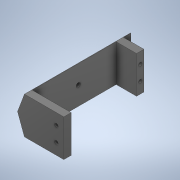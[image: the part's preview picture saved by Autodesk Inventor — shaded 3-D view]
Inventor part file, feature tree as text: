
AUTODESK INVENTOR PART (.ipt)
format: ipt  version: 2020 (Build 240168000, 168)  size: 239,616 bytes
history: native  units: in
note: dims shown in document units (in); Inventor stores cm internally (conversion verified against a paired STEP export)
features: sketch x9, extrude x7, projected_geometry x3, plane x1, loft x1
ambient origin geometry x8: Origin, YZ Plane, XZ Plane, XY Plane, X Axis, Y Axis, Z Axis, Center Point
bodies: Solid1 (feature_tree)
feature tree (21):
  sketch  "Sketch1"  dims[d1=1.1811in d2=3.3858in]
  plane  "Work Plane1"
  loft  "Loft1"
  extrude  "Extrusion1"  Depth=1.1811in
  extrude  "Extrusion2"  TaperAngle=0.0deg  [1 undecoded]
  extrude  "Extrusion3"  Depth=0.2362in
  extrude  "Extrusion4"  Depth=0.2362in
  extrude  "Extrusion5"  TaperAngle=0.0deg  [1 undecoded]
  extrude  "Extrusion6"  Depth=0.1378in
  extrude  "Extrusion7"  Depth=0.1378in
  sketch  "Sketch2"  dims[d3=1.1811in d5=0.5906in]
  sketch  "Sketch3"  dims[d6=0.5906in d7=0.0in d8=90.0deg]
  sketch  "Sketch4"  dims[d9=0.0in d10=90.0deg d11=0.2362in]
  sketch  "Sketch5"  dims[d12=0.2362in d13=0.2362in]
  projected_geometry  "Projected Loop1"
  sketch  "Sketch6"  dims[d14=0.65in d15=0.0in]
  projected_geometry  "Projected Loop2"
  sketch  "Sketch8"  dims[d16=1.7028in d17=0.1378in]
  sketch  "Sketch9"  dims[d18=0.0in d19=0.0in d20=0.1378in]
  sketch  "Sketch10"  dims[d21=0.1181in d22=0.0in d23=0.4724in d24=0.0in d25=0.1181in d26=0.1181in d27=0.2362in d28=0.2362in d29=0.1142in d30=0.1142in d31=0.2756in d32=0.0in d33=0.2362in d35=0.1181in d36=0.1181in d41=0.2756in d42=0.0in d43=0.1181in d44=0.2362in d45=0.2362in d46=0.1142in d47=0.1142in d48=0.1181in d49=0.1181in d50=0.0157in d51=0.5906in d52=0.0157in d53=0.2362in d54=0.1181in d55=0.0in d4=0.0197in]
  projected_geometry  "Projected Loop5"
note: 2 required parameter values undecoded (feature->parameter linkage not recoverable at this tier; creation-order binding heuristic only, values carry confidence <= 0.55)
